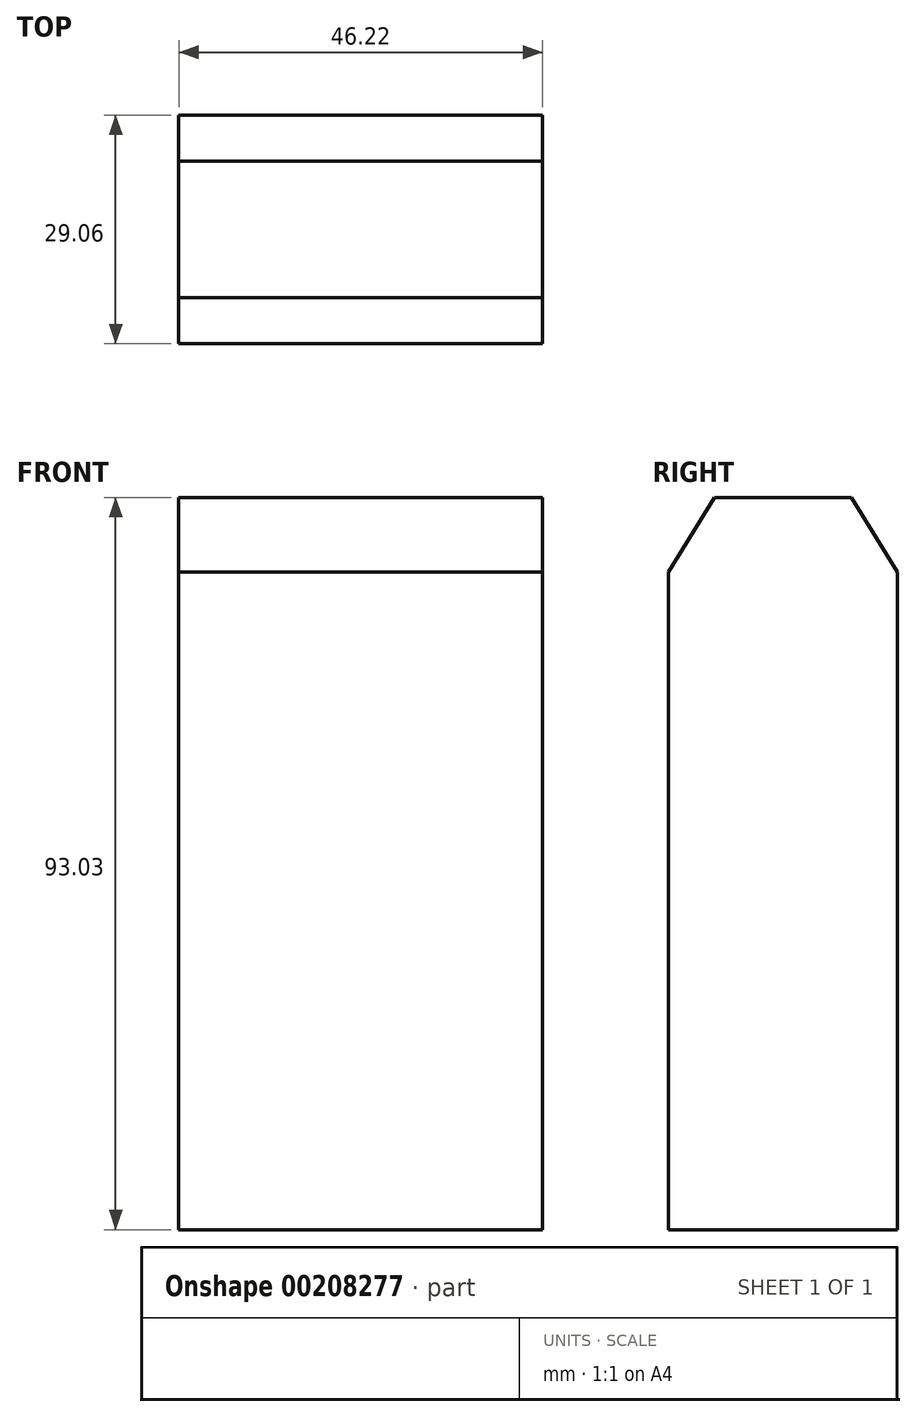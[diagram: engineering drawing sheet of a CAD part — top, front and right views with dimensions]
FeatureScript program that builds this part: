
annotation { "Feature Type Name" : "Feature", "Feature Type Description" : "" }
export const myFeature = defineFeature(function(context is Context, id is Id, definition is map)
    precondition{}
    {
        {
            var Q0;
            Q0=qCreatedBy(makeId("Right.planeOp"),FACE);
            var sketch = newSketch(context, id + "F0", { "sketchPlane" : qUnion([Q0])});
            skLineSegment(sketch, "E0.bottom", {"start": v(14.53, -41.47) * mm, "end": v(-14.53, -41.47) * mm});
            skLineSegment(sketch, "E0.top", {"start": v(14.53, 27.54) * mm, "end": v(-14.53, 27.54) * mm});
            skLineSegment(sketch, "E0.left", {"start": v(14.53, -41.47) * mm, "end": v(14.53, 27.54) * mm});
            skLineSegment(sketch, "E0.right", {"start": v(-14.53, -41.47) * mm, "end": v(-14.53, 27.54) * mm});
            skPoint(sketch, "E0.middle", {"position": v(0, -6.96) * mm});
            skLineSegment(sketch, "E1", {"start": v(-14.53, 27.54) * mm, "end": v(-14.53, 42.07) * mm});
            skLineSegment(sketch, "E2", {"start": v(-14.53, 42.07) * mm, "end": v(-8.68, 51.56) * mm});
            skLineSegment(sketch, "E3", {"start": v(-8.68, 51.56) * mm, "end": v(0, 51.56) * mm});
            skLineSegment(sketch, "E4.MirrorCS", {"start": v(8.68, 51.56) * mm, "end": v(0, 51.56) * mm});
            skLineSegment(sketch, "E5.MirrorCS", {"start": v(14.53, 42.07) * mm, "end": v(8.68, 51.56) * mm});
            skLineSegment(sketch, "E6.MirrorCS", {"start": v(14.53, 27.54) * mm, "end": v(14.53, 42.07) * mm});
            skSolve(sketch);
        }
        {
            var Q0;
            Q0=makeQuery(id+"F0.imprint","IMPRINT",FACE,{"disambiguationData":[TD([[makeQuery(id+"F0.imprint","IMPRINT",EDGE,{"derivedFrom":sQuery(id+"F0.wireOp",EDGE,"E0.bottom")}),-1.0]])]});
            var Q1;
            Q1=makeQuery(id+"F0.imprint","IMPRINT",FACE,{"disambiguationData":[TD([[makeQuery(id+"F0.imprint","IMPRINT",EDGE,{"derivedFrom":sQuery(id+"F0.wireOp",EDGE,"E0.top")}),-1.0]])]});
            extrude(context, id + "F1", {"entities" : qUnion([Q0, Q1]), "endBound" : BoundingType.SYMMETRIC, "depth" : 46.23 * mm});
        }
    });
